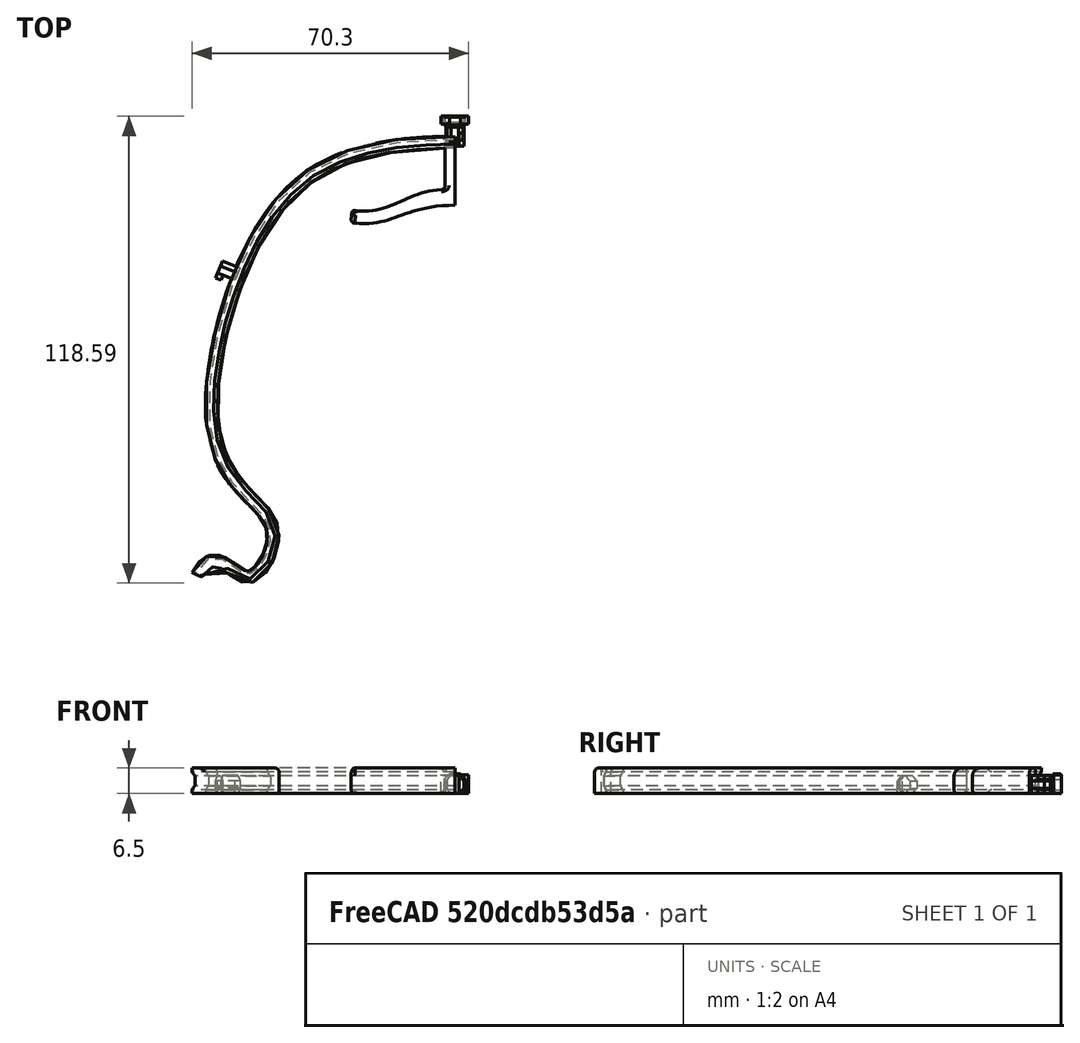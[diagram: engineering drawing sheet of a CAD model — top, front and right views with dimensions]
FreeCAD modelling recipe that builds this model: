
FCSTD DOCUMENT  (FreeCAD 0.18R16146 (Git))
Label: frame-001-02-b
License: All rights reserved
LicenseURL: http://ja.wikipedia.org/wiki/%E8%91%97%E4%BD%9C%E6%A8%A9%E8%A1%A8%E7%A4%BA
objects: Sketcher::SketchObject×5, Part::Extrusion×5, Part::Box×3, Part::Cut×2, Part::Fillet×2, Part::Compound×2, Mesh::Feature×1, Part::Sweep×1, Part::Mirroring×1, Part::MultiCommon×1
note: 22 computed .brp shape members not serialized (recipe doc carries the construction recipe); baked Part::Feature solids carry a one-line shape summary decoded from their .brp

FEATURE [Sketcher::SketchObject] Sketch  label="Sketch_FrameShape"
  sketch-geometry (15):
    g0-g7: Circle [constr] x8 (B-spline internal-alignment scaffolding for g8; pole/knot coordinates omitted)
    g8: BSplineCurve PolesCount=8 KnotsCount=6 Degree=3 IsPeriodic=0
    g9-g14: GeomPoint [constr] x6 (B-spline internal-alignment scaffolding for g8; pole/knot coordinates omitted)
  constraints (6):
    c: Radius(g0) = 6
    c: Equal(g0, g1-g6) x6
    c: InternalAlignment(g0-g7 -> g8) x8
    c: InternalAlignment(g9-g14 -> g8) x6
    c: Horizontal(g1,g8)
    c: Coincident(g-1,g8)
FEATURE [Sketcher::SketchObject] Sketch001
  Placement = pos=(0,0,0) rot=(0.57735,0.57735,0.57735;2.0944rad)
  sketch-geometry (8):
    g0: LineSegment StartX=-0.5 StartY=6.5 StartZ=0 EndX=2.5 EndY=6.5 EndZ=0
    g1: LineSegment StartX=2.5 StartY=6.5 StartZ=0 EndX=2.5 EndY=5.5 EndZ=0
    g2: LineSegment StartX=2.5 StartY=0 StartZ=0 EndX=-0.5 EndY=0 EndZ=0
    g3: LineSegment StartX=-0.5 StartY=0 StartZ=0 EndX=-0.5 EndY=6.5 EndZ=0
    g4: LineSegment StartX=2.5 StartY=5.5 StartZ=0 EndX=1.7 EndY=4.5 EndZ=0
    g5: LineSegment StartX=1.7 StartY=4.5 StartZ=0 EndX=1.7 EndY=2 EndZ=0
    g6: LineSegment StartX=1.7 StartY=2 StartZ=0 EndX=2.5 EndY=1 EndZ=0
    g7: LineSegment StartX=2.5 StartY=1 StartZ=0 EndX=2.5 EndY=0 EndZ=0
  constraints (24):
    c: Coincident(g0,g1)
    c: Coincident(g2,g3)
    c: Coincident(g3,g0)
    c: Horizontal(g0)
    c: Horizontal(g2)
    c: Vertical(g1)
    c: Vertical(g3)
    c: DistanceX(g0,g0) = 3
    c: DistanceY(g1,g0) = 1
    c: DistanceX(g-1,g2) = -0.5
    c: PointOnObject(g2,g-1)
    c: DistanceY(g2,g0) = 6.5
    c: Coincident(g1,g4)
    c: Coincident(g4,g5)
    c: Vertical(g5)
    c: Coincident(g5,g6)
    c: Coincident(g6,g7)
    c: Coincident(g7,g2)
    c: DistanceX(g2,g2) = 3
    c: Vertical(g7)
    c: DistanceY(g2,g6) = 1
    c: DistanceY(g6,g5) = 1
    c: DistanceY(g4,g1) = 1
    c: DistanceX(g2,g5) = 2.2
FEATURE [Mesh::Feature] cd43cbcc_75a4_11ea_893f_42010a00001e_UM3E_Visor_frame_EUROPE_ISO838_v3  label="cd43cbcc-75a4-11ea-893f-42010a00001e_UM3E_Visor_frame_EUROPE_ISO838_v3"
  Placement = pos=(0,-59,0) rot=(0,0,1;0rad)
FEATURE [Sketcher::SketchObject] Sketch002  label="OctPinSketch"
  Placement = pos=(0,0,0) rot=(1,0,0;1.5708rad)
  sketch-geometry (9):
    g0: LineSegment StartX=2.3097 StartY=1.35299 StartZ=0 EndX=2.3097 EndY=3.26641 EndZ=0
    g1: LineSegment StartX=2.3097 StartY=3.26641 StartZ=0 EndX=0.956709 EndY=4.6194 EndZ=0
    g2: LineSegment StartX=0.956709 StartY=4.6194 StartZ=0 EndX=-0.956709 EndY=4.6194 EndZ=0
    g3: LineSegment StartX=-0.956709 StartY=4.6194 StartZ=0 EndX=-2.3097 EndY=3.26641 EndZ=0
    g4: LineSegment StartX=-2.3097 StartY=3.26641 StartZ=0 EndX=-2.3097 EndY=1.35299 EndZ=0
    g5: LineSegment StartX=-2.3097 StartY=1.35299 StartZ=0 EndX=-0.956709 EndY=0 EndZ=0
    g6: LineSegment StartX=-0.956709 StartY=0 StartZ=0 EndX=0.956709 EndY=0 EndZ=0
    g7: LineSegment StartX=0.956709 StartY=0 StartZ=0 EndX=2.3097 EndY=1.35299 EndZ=0
    g8: Circle [constr] CenterX=0 CenterY=2.3097 CenterZ=0 NormalX=0 NormalY=0 NormalZ=1 AngleXU=0 Radius=2.5
  constraints (21):
    c: Coincident(g0,g1)
    c: Coincident(g1,g2)
    c: Coincident(g2,g3)
    c: Coincident(g3,g4)
    c: Coincident(g4,g5)
    c: Coincident(g5,g6)
    c: Coincident(g6,g7)
    c: Coincident(g7,g0)
    c: Equal(g0, g1-g7) x7
    c: PointOnObject(g0,g8)
    c: PointOnObject(g1,g8)
    c: PointOnObject(g2,g8)
    c: PointOnObject(g3,g8)
    c: PointOnObject(g4,g8)
    c: PointOnObject(g5,g8)
    c: PointOnObject(g6,g8)
    c: PointOnObject(g7,g8)
    c: Distance(g0,g8) = 2.5
    c: Horizontal(g6)
    c: PointOnObject(g8,g-2)
    c: PointOnObject(g6,g-1)
FEATURE [Part::Extrusion] Extrude002  label="OctPin"
  Base = -> Sketch002
  Dir = (0,-1,0)
  DirMode = 2
  FaceMakerClass = Part::FaceMakerBullseye
  LengthFwd = -6
  LengthRev = 0
  Solid = true
  Symmetric = false
FEATURE [Part::Extrusion] Extrude003  label="OctPinFront"
  Base = -> Sketch002
  Dir = (0,-1,2e-16)
  DirMode = 2
  FaceMakerClass = Part::FaceMakerBullseye
  LengthFwd = -3.8
  LengthRev = 0
  Placement = pos=(0,3,0) rot=(0,0,1;0rad)
  Solid = true
  Symmetric = false
FEATURE [Part::Extrusion] Extrude004  label="OctPin_WNotch_column"
  Base = -> Sketch002
  Dir = (0,-1,2e-16)
  DirMode = 2
  FaceMakerClass = Part::FaceMakerBullseye
  LengthFwd = -4.8
  LengthRev = 0
  Solid = true
  Symmetric = false
FEATURE [Part::Box] Box008  label="立方体008"
  AttacherType = Attacher::AttachEngine3D
  Height = 6
  Length = 2
  Placement = pos=(1,0,-0.5) rot=(0,0,1;0rad)
  Width = 3.3
FEATURE [Part::Cut] Cut  label="OctPin_WNotch"
  Base = -> Extrude004
  Tool = -> Box008
FEATURE [Part::Cut] Cut001  label="OctPin_WNotchR"
  Base = -> Extrude004
  Placement = pos=(55.5,-33.1,0) rot=(0,0,-1;1.18682rad)
  Tool = -> Box008
FEATURE [Sketcher::SketchObject] Sketch003
  sketch-geometry (18):
    g0: LineSegment StartX=0 StartY=1 StartZ=0 EndX=0 EndY=-15 EndZ=0
    g1: LineSegment StartX=2.5 StartY=-11 StartZ=0 EndX=2.5 EndY=1 EndZ=0
    g2: LineSegment StartX=2.5 StartY=1 StartZ=0 EndX=0 EndY=1 EndZ=0
    g3: LineSegment StartX=26.0693 StartY=-16.3 StartZ=0 EndX=26.4803 EndY=-19.4735 EndZ=0
    g4-g7: Circle [constr] x4 (B-spline internal-alignment scaffolding for g8; pole/knot coordinates omitted)
    g8: BSplineCurve PolesCount=4 KnotsCount=2 Degree=3 IsPeriodic=0
    g9: GeomPoint [constr] X=2.5 Y=-11 Z=0
    g10: GeomPoint [constr] X=26.0693 Y=-16.3 Z=0
    g11-g14: Circle [constr] x4 (B-spline internal-alignment scaffolding for g15; pole/knot coordinates omitted)
    g15: BSplineCurve PolesCount=4 KnotsCount=2 Degree=3 IsPeriodic=0
    g16: GeomPoint [constr] X=0 Y=-15 Z=0
    g17: GeomPoint [constr] X=26.4803 Y=-19.4735 Z=0
  constraints (32):
    c: PointOnObject(g0,g-2)
    c: Vertical(g0)
    c: Vertical(g1)
    c: Coincident(g1,g2)
    c: Coincident(g2,g0)
    c: DistanceX(g0,g1) = 2.5
    c: Horizontal(g2)
    c: DistanceY(g-1,g0) = 1
    c: DistanceY(g3,g1) = 5.3
    c: DistanceY(g0,g1) = 4
    c: DistanceY(g0,g-1) = 15
    c: Coincident(g8,g1)
    c: Radius(g4) = 2
    c: Equal(g4,g5)
    c: Equal(g4,g6)
    c: Equal(g4,g7)
    c: Coincident(g8,g3)
    c: InternalAlignment(g4-g7 -> g8) x4
    c: InternalAlignment(g9,g8)
    c: InternalAlignment(g10,g8)
    c: Coincident(g15,g0)
    c: Radius(g11) = 2
    c: Equal(g11,g12)
    c: Equal(g11,g13)
    c: Equal(g11,g14)
    c: Coincident(g15,g3)
    c: InternalAlignment(g11-g14 -> g15) x4
    c: InternalAlignment(g16,g15)
    c: InternalAlignment(g17,g15)
    c: Distance(g3,g3) = 3.2
    c: Horizontal(g0,g12)
    c: Horizontal(g5,g1)
FEATURE [Part::Extrusion] Extrude
  Base = -> Sketch003
  Dir = (0,0,1)
  DirMode = 2
  FaceMakerClass = Part::FaceMakerBullseye
  LengthFwd = 6.5
  LengthRev = 0
  Solid = true
  Symmetric = false
FEATURE [Part::Fillet] Fillet  label="AGOATE_R"
  Base = -> Extrude
  Edges = 11 edges: [Edge1 r=1,Edge3 r=1,Edge4 r=1,Edge11 r=1,Edge12 r=1,Edge13 r=2,Edge14 r=0.5,Edge15 r=1,Edge16 r=1,Edge17 r=0.5,Edge18 r=0.5]
FEATURE [Part::Sweep] Sweep  label="Sweep_RightFrame"
  Frenet = false
  Sections = -> [Sketch001]
  Solid = true
  Spine = -> Sketch [Edge1]
  Transition = 1
FEATURE [Part::Fillet] Fillet001  label="Fillet_Sweep_RightFrame"
  Base = -> Sweep
  Edges = 2 edges r=1: [Edge1,Edge24]
FEATURE [Part::Compound] Compound  label="RightSide"
  Links = -> [Cut001,Fillet,Fillet001]
FEATURE [Part::Mirroring] Part__Mirroring001  label="LeftSide (Mirrored)"
  Base = (0,0,0)
  Normal = (1,0,0)
  Source = -> Compound
FEATURE [Part::Box] Box  label="立方体"
  AttacherType = Attacher::AttachEngine3D
  Height = 10
  Length = 4
  Placement = pos=(-2,2.8,0) rot=(0,0,1;0rad)
  Width = 4
FEATURE [Part::Box] Box010  label="立方体010"
  AttacherType = Attacher::AttachEngine3D
  Height = 4.7
  Length = 7
  Placement = pos=(-3.5,5.6,0) rot=(0,0,1;0rad)
  Width = 2
FEATURE [Part::MultiCommon] Common  label="前ダボ柱"
  Shapes = -> [Extrude003,Box]
FEATURE [Sketcher::SketchObject] Sketch004
  MapMode = 5
  Placement = pos=(0,6.8,0) rot=(0,0.707107,0.707107;3.14159rad)
  Support = -> [Common]
  sketch-geometry (8):
    g0: LineSegment StartX=-2.34451 StartY=0 StartZ=0 EndX=-2.75 EndY=1.00428 EndZ=0
    g1: LineSegment StartX=-2.75 StartY=1.00428 StartZ=0 EndX=-2.75 EndY=3.6504 EndZ=0
    g2: LineSegment StartX=-2.75 StartY=3.6504 StartZ=0 EndX=-1.4004 EndY=5 EndZ=0
    g3: LineSegment StartX=-1.4004 StartY=5 StartZ=0 EndX=1.4004 EndY=5 EndZ=0
    g4: LineSegment StartX=1.4004 StartY=5 StartZ=0 EndX=2.75 EndY=3.6504 EndZ=0
    g5: LineSegment StartX=2.75 StartY=3.6504 StartZ=0 EndX=2.75 EndY=1.00428 EndZ=0
    g6: LineSegment StartX=2.75 StartY=1.00428 StartZ=0 EndX=2.34451 EndY=0 EndZ=0
    g7: LineSegment StartX=2.34451 StartY=0 StartZ=0 EndX=-2.34451 EndY=0 EndZ=0
  constraints (17):
    c: Coincident(g0,g1)
    c: Coincident(g1,g2)
    c: Coincident(g2,g3)
    c: Coincident(g3,g4)
    c: Coincident(g4,g5)
    c: Coincident(g5,g6)
    c: Coincident(g6,g7)
    c: Coincident(g7,g0)
    c: Vertical(g1)
    c: Symmetric(g0,g6,g-2)
    c: Symmetric(g0,g5,g-2)
    c: Symmetric(g1,g4,g-2)
    c: Symmetric(g2,g3,g-2)
    c: PointOnObject(g6,g-1)
    c: DistanceY(g6,g3) = 5
    c: DistanceX(g0,g5) = 5.5
    c: Angle(g5,g4,g4) = 0.785398
FEATURE [Part::Extrusion] Extrude005  label="前ダボトメ"
  Base = -> Sketch004
  Dir = (0,1,-2e-16)
  DirMode = 2
  FaceMakerClass = Part::FaceMakerBullseye
  LengthFwd = 2
  LengthRev = 0
  Solid = true
  Symmetric = false
FEATURE [Part::Compound] Compound001  label="前ダボ"
  Links = -> [Common,Extrude005]
  Placement = pos=(0,-1.4,0) rot=(0,0,1;0rad)
